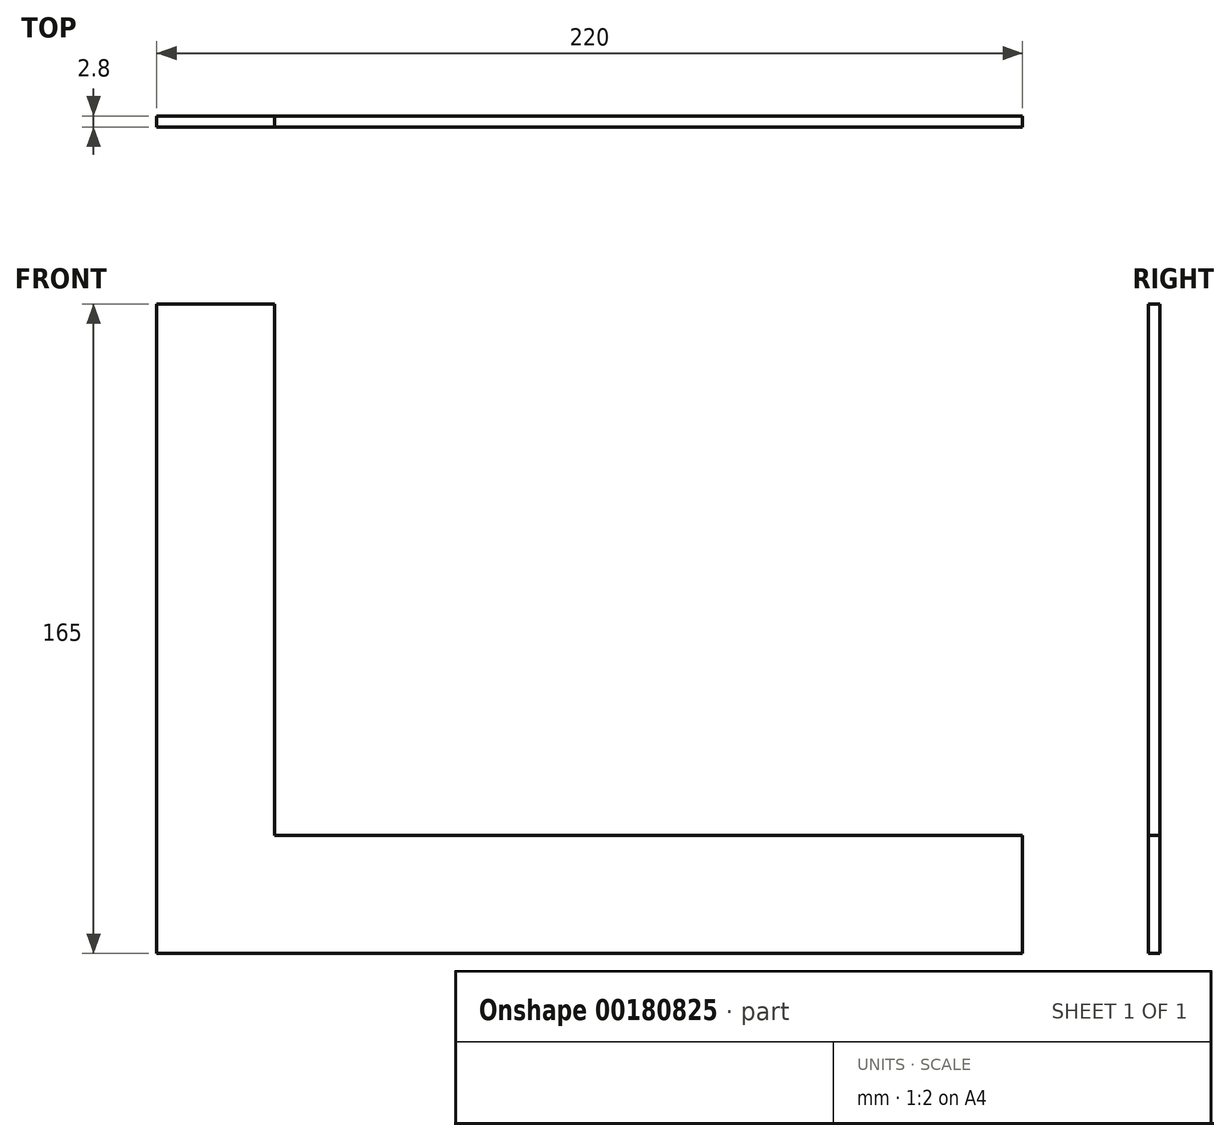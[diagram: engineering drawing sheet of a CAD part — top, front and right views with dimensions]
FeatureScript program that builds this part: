
annotation { "Feature Type Name" : "Feature", "Feature Type Description" : "" }
export const myFeature = defineFeature(function(context is Context, id is Id, definition is map)
    precondition{}
    {
        {
            var Q0;
            Q0=qCreatedBy(makeId("Front.planeOp"),FACE);
            var sketch = newSketch(context, id + "F0", { "sketchPlane" : qUnion([Q0])});
            skLineSegment(sketch, "E0.bottom", {"start": v(0, 0) * mm, "end": v(220, 0) * mm});
            skLineSegment(sketch, "E0.top", {"start": v(0, -30) * mm, "end": v(220, -30) * mm});
            skLineSegment(sketch, "E0.left", {"start": v(0, 0) * mm, "end": v(0, -30) * mm});
            skLineSegment(sketch, "E0.right", {"start": v(220, 0) * mm, "end": v(220, -30) * mm});
            skLineSegment(sketch, "E1.bottom", {"start": v(0, -30) * mm, "end": v(30, -30) * mm});
            skLineSegment(sketch, "E1.top", {"start": v(0, 135) * mm, "end": v(30, 135) * mm});
            skLineSegment(sketch, "E1.left", {"start": v(0, -30) * mm, "end": v(0, 135) * mm});
            skLineSegment(sketch, "E1.right", {"start": v(30, -30) * mm, "end": v(30, 135) * mm});
            skSolve(sketch);
        }
        {
            var Q0;
            Q0 = qSketchRegion(id + "F0", true);
            extrude(context, id + "F1", {"entities" : qUnion([Q0]), "depth" : 2.8 * mm});
        }
    });
